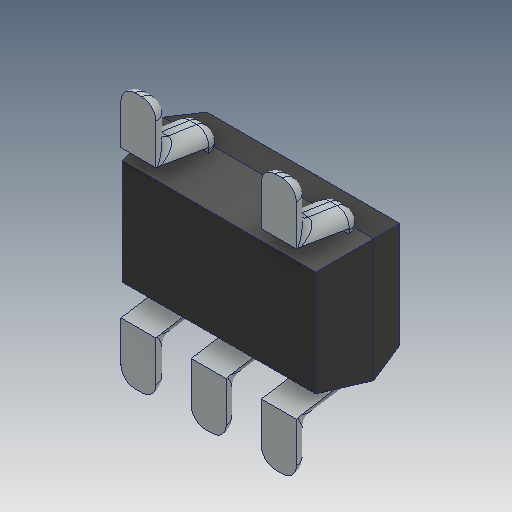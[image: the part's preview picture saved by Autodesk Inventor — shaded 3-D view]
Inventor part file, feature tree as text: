
AUTODESK INVENTOR PART (.ipt)
format: ipt  version: 2018 (Build 220112000, 112)  size: 262,656 bytes
history: native  units: mm
features: fillet x1
ambient origin geometry x8: Origin, YZ Plane, XZ Plane, XY Plane, X Axis, Y Axis, Z Axis, Center Point
bodies: Volumenkörper1 (feature_tree)
feature tree (1):
  fillet  "Fillet6"  [1 undecoded]
note: 1 required parameter value undecoded (feature->parameter linkage not recoverable at this tier; creation-order binding heuristic only, values carry confidence <= 0.55)
